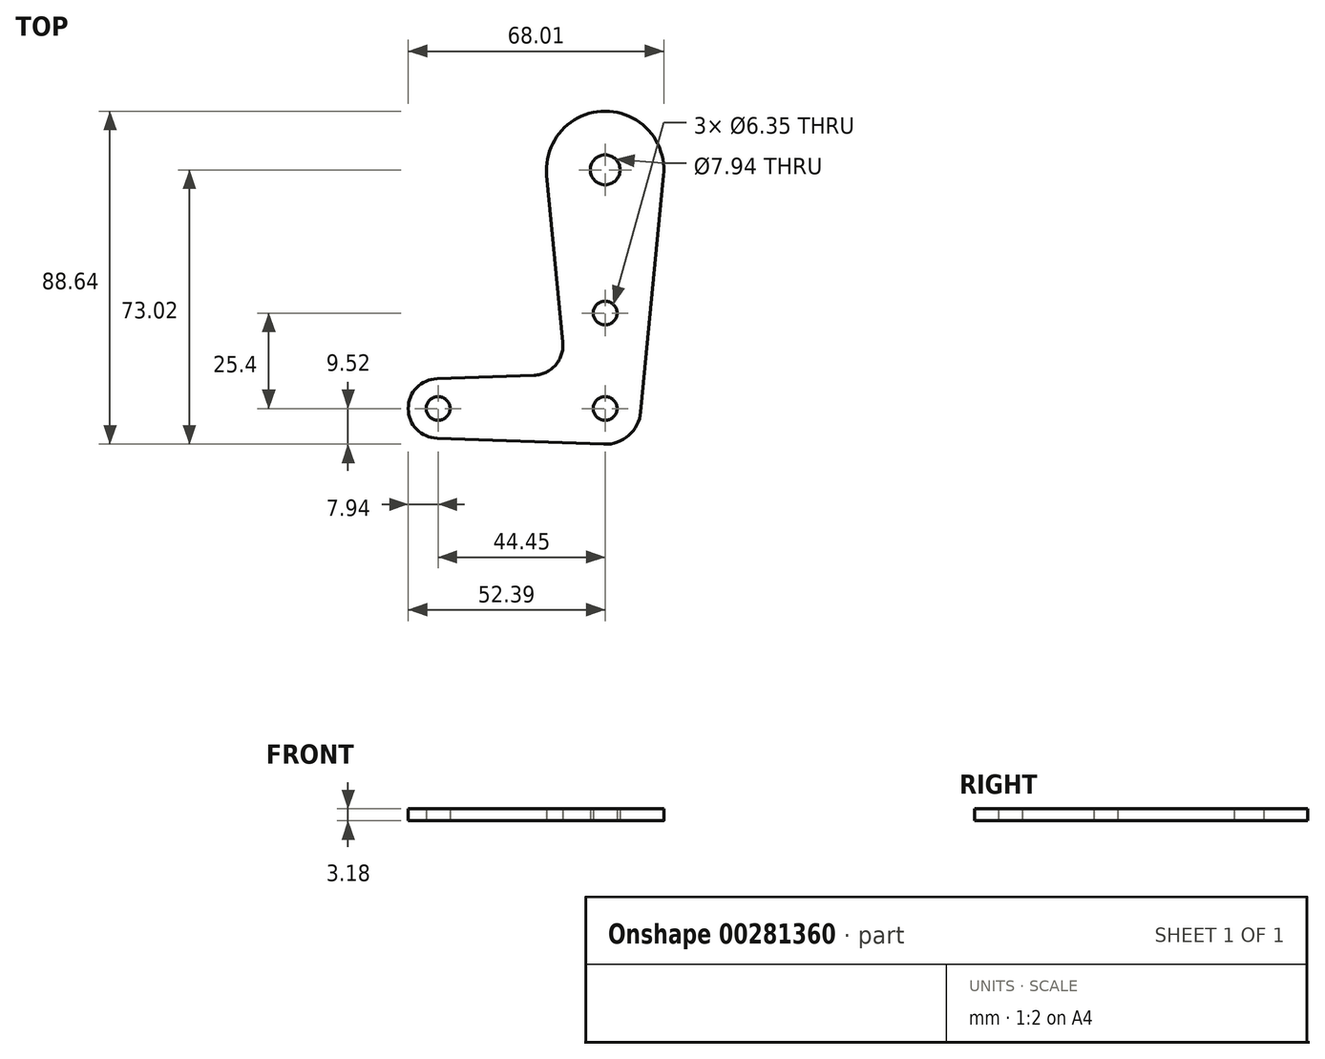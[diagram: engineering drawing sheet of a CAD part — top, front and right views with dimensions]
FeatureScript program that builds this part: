
annotation { "Feature Type Name" : "Feature", "Feature Type Description" : "" }
export const myFeature = defineFeature(function(context is Context, id is Id, definition is map)
    precondition{}
    {
        {
            var Q0;
            Q0=qCreatedBy(makeId("Top.planeOp"),FACE);
            var sketch = newSketch(context, id + "F0", { "sketchPlane" : qUnion([Q0])});
            skCircle(sketch, "E0", {"center": v(0, 0) * mm, "radius": 3.18 * mm});
            skCircle(sketch, "E1", {"center": v(-44.45, 0) * mm, "radius": 3.18 * mm});
            skCircle(sketch, "E2", {"center": v(0, 0) * mm, "radius": 9.53 * mm});
            skCircle(sketch, "E3", {"center": v(-44.45, 0) * mm, "radius": 7.94 * mm});
            skLineSegment(sketch, "E4", {"start": v(-44.73, -7.93) * mm, "end": v(-0.34, -9.52) * mm});
            skCircle(sketch, "E5", {"center": v(0, 63.5) * mm, "radius": 3.97 * mm});
            skCircle(sketch, "E6", {"center": v(0, 63.5) * mm, "radius": 15.62 * mm});
            skLineSegment(sketch, "E7", {"start": v(15.55, 62) * mm, "end": v(9.48, -0.91) * mm});
            skLineSegment(sketch, "E8", {"start": v(-15.55, 62) * mm, "end": v(-11.26, 17.55) * mm});
            skLineSegment(sketch, "E9", {"start": v(-44.73, 7.93) * mm, "end": v(-18.88, 8.86) * mm});
            skArc(sketch, "E10.filletArc", {"start": v(-18.88, 8.86) * mm, "mid": v(-13.2, 11.56) * mm, "end": v(-11.26, 17.55) * mm});
            skLineSegment(sketch, "E11", {"start": v(0, 79.12) * mm, "end": v(0, -9.53) * mm, "construction": true});
            skPoint(sketch, "E12.orphan", {"position": v(0, 95.62) * mm});
            skCircle(sketch, "E13", {"center": v(0, 25.4) * mm, "radius": 3.18 * mm});
            skSolve(sketch);
        }
        {
            var Q0;
            Q0 = qSketchRegion(id + "F0", true);
            extrude(context, id + "F1", {"entities" : qUnion([Q0]), "depth" : 3.17 * mm});
        }
    });
